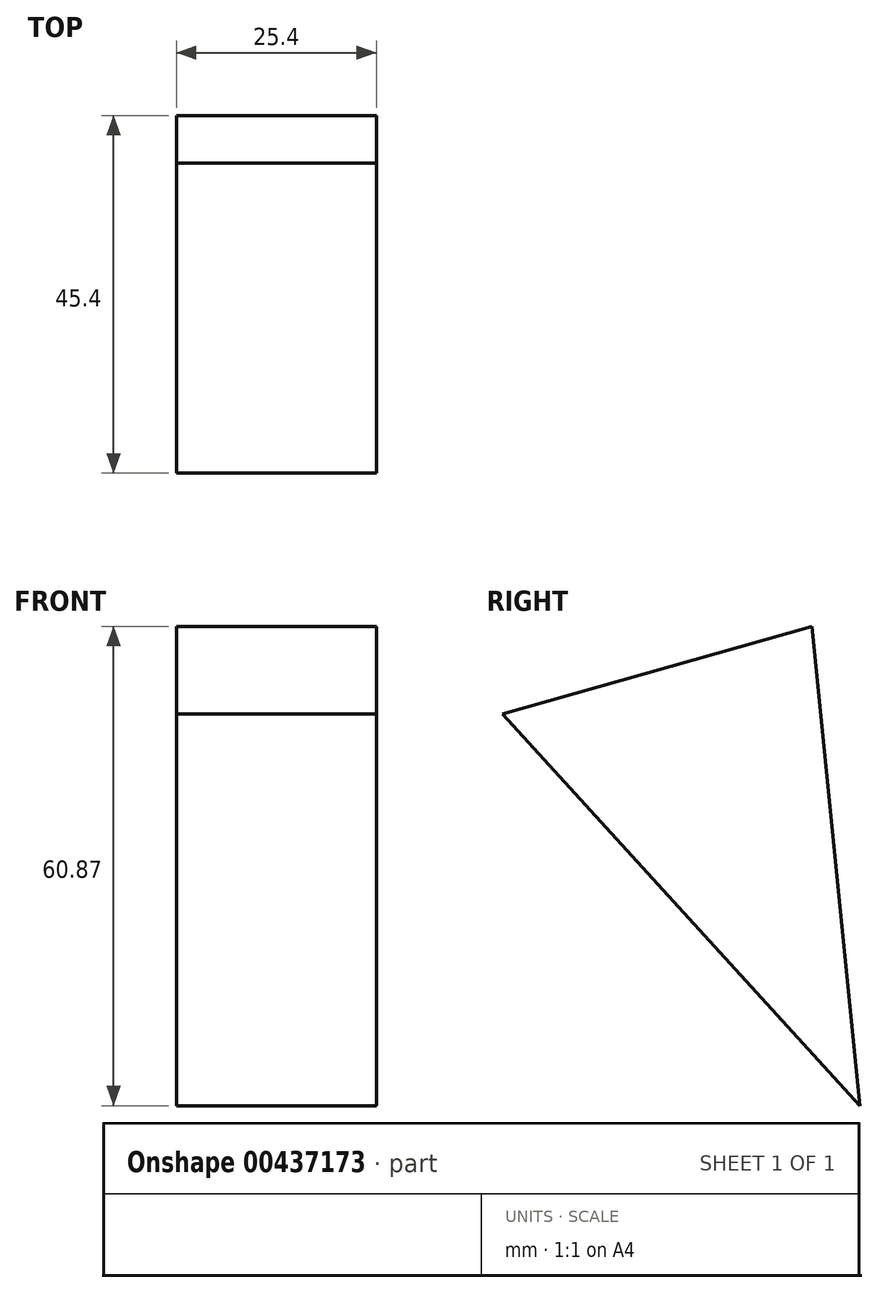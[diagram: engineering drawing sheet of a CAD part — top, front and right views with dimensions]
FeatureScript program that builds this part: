
annotation { "Feature Type Name" : "Feature", "Feature Type Description" : "" }
export const myFeature = defineFeature(function(context is Context, id is Id, definition is map)
    precondition{}
    {
        {
            var Q0;
            Q0=qCreatedBy(makeId("Right.planeOp"),FACE);
            var sketch = newSketch(context, id + "F0", { "sketchPlane" : qUnion([Q0])});
            skLineSegment(sketch, "E0", {"start": v(-45.4, 49.78) * mm, "end": v(0, 0) * mm});
            skLineSegment(sketch, "E1", {"start": v(0, 0) * mm, "end": v(-6.05, 60.87) * mm});
            skLineSegment(sketch, "E2", {"start": v(-6.05, 60.87) * mm, "end": v(-45.4, 49.78) * mm});
            skSolve(sketch);
        }
        {
            var Q0;
            Q0=makeQuery(id+"F0.imprint","IMPRINT",FACE,{"disambiguationData":[TD([[makeQuery(id+"F0.imprint","IMPRINT",EDGE,{"derivedFrom":sQuery(id+"F0.wireOp",EDGE,"E0")}),1.0]])]});
            extrude(context, id + "F1", {"entities" : qUnion([Q0]), "oppositeDirection" : true, "depth" : 25.4 * mm});
        }
    });
